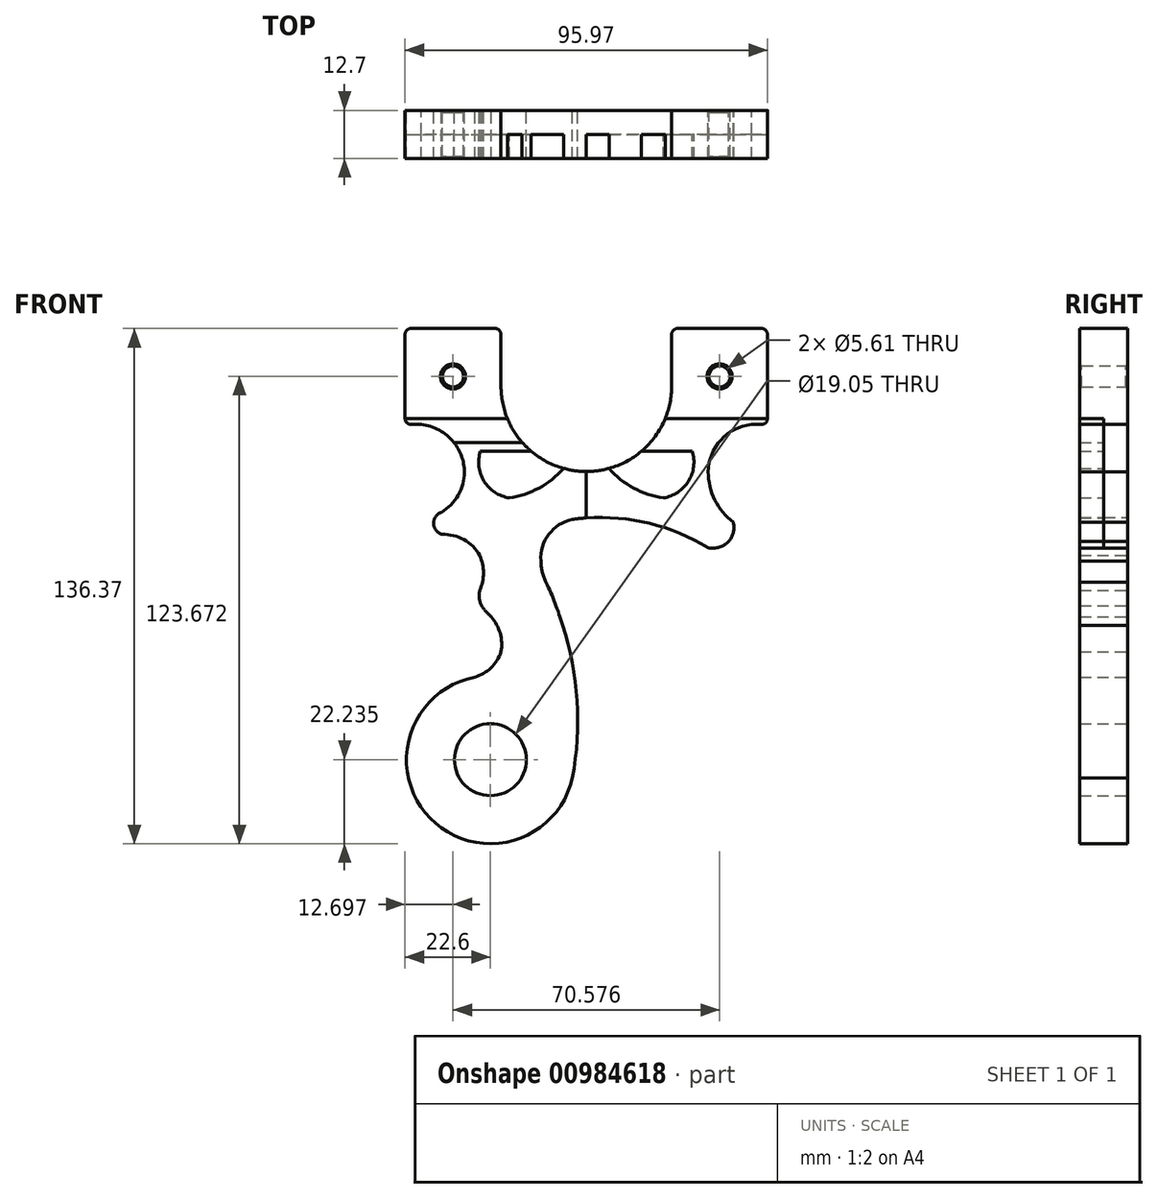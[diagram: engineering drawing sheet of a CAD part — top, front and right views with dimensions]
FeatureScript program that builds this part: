
annotation { "Feature Type Name" : "Feature", "Feature Type Description" : "" }
export const myFeature = defineFeature(function(context is Context, id is Id, definition is map)
    precondition{}
    {
        {
            var Q0;
            Q0=qCreatedBy(makeId("Front.planeOp"),FACE);
            var sketch = newSketch(context, id + "F0", { "sketchPlane" : qUnion([Q0])});
            skCircle(sketch, "E0", {"center": v(-13.36, -38.22) * mm, "radius": 9.53 * mm});
            skLineSegment(sketch, "E1", {"start": v(-35.96, 52.1) * mm, "end": v(-35.96, 74.33) * mm});
            skLineSegment(sketch, "E2.bottom", {"start": v(-34.38, 75.92) * mm, "end": v(-12.15, 75.92) * mm});
            skLineSegment(sketch, "E2.top", {"start": v(-34.38, 50.52) * mm, "end": v(-31.71, 50.52) * mm});
            skLineSegment(sketch, "E2.left", {"start": v(-35.96, 74.33) * mm, "end": v(-35.96, 52.1) * mm});
            skLineSegment(sketch, "E2.right", {"start": v(-10.56, 74.33) * mm, "end": v(-10.56, 60.66) * mm});
            skArc(sketch, "E3", {"start": v(-10.56, 60.66) * mm, "mid": v(-3.95, 44.68) * mm, "end": v(12.03, 38.07) * mm});
            skLineSegment(sketch, "E4", {"start": v(-23.26, 60.42) * mm, "end": v(-23.26, 66.03) * mm});
            skLineSegment(sketch, "E5", {"start": v(-26.07, 63.22) * mm, "end": v(-20.46, 63.22) * mm});
            skCircle(sketch, "E6", {"center": v(-23.26, 63.22) * mm, "radius": 2.8 * mm});
            skCircle(sketch, "E7.MirrorC", {"center": v(47.31, 63.22) * mm, "radius": 2.8 * mm});
            skLineSegment(sketch, "E8.MirrorCS", {"start": v(47.31, 60.42) * mm, "end": v(47.31, 66.03) * mm});
            skLineSegment(sketch, "E9.MirrorCS", {"start": v(50.12, 63.22) * mm, "end": v(44.5, 63.22) * mm});
            skLineSegment(sketch, "E10.MirrorCS", {"start": v(60.01, 74.33) * mm, "end": v(60.01, 52.1) * mm});
            skLineSegment(sketch, "E11.MirrorCS", {"start": v(58.43, 75.92) * mm, "end": v(36.2, 75.92) * mm});
            skLineSegment(sketch, "E12.MirrorCS", {"start": v(34.61, 74.33) * mm, "end": v(34.61, 60.66) * mm});
            skLineSegment(sketch, "E13.MirrorCS", {"start": v(58.43, 50.52) * mm, "end": v(55.76, 50.52) * mm});
            skArc(sketch, "E14.MirrorCS", {"start": v(34.61, 60.66) * mm, "mid": v(28, 44.68) * mm, "end": v(12.03, 38.07) * mm});
            skArc(sketch, "E15", {"start": v(-35.96, 52.1) * mm, "mid": v(-35.5, 50.99) * mm, "end": v(-34.38, 50.52) * mm});
            skArc(sketch, "E16.MirrorC", {"start": v(-35.96, 74.33) * mm, "mid": v(-35.5, 75.46) * mm, "end": v(-34.38, 75.92) * mm});
            skArc(sketch, "E17.MirrorC", {"start": v(-10.56, 74.33) * mm, "mid": v(-11.03, 75.46) * mm, "end": v(-12.15, 75.92) * mm});
            skPoint(sketch, "E18.orphan", {"position": v(-35.96, 75.92) * mm});
            skPoint(sketch, "E19.orphan", {"position": v(-35.96, 50.52) * mm});
            skPoint(sketch, "E20.orphan", {"position": v(-10.56, 75.92) * mm});
            skLineSegment(sketch, "E21.trimOffspring", {"start": v(-12.15, 75.92) * mm, "end": v(-34.38, 75.92) * mm});
            skArc(sketch, "E22.MirrorCS", {"start": v(60.01, 74.33) * mm, "mid": v(59.55, 75.46) * mm, "end": v(58.43, 75.92) * mm});
            skArc(sketch, "E23.MirrorCS", {"start": v(34.61, 74.33) * mm, "mid": v(35.08, 75.46) * mm, "end": v(36.2, 75.92) * mm});
            skArc(sketch, "E24.MirrorCS", {"start": v(60.01, 52.1) * mm, "mid": v(59.55, 50.99) * mm, "end": v(58.43, 50.52) * mm});
            skPoint(sketch, "E25.orphan", {"position": v(34.61, 75.92) * mm});
            skPoint(sketch, "E26.orphan", {"position": v(60.01, 75.92) * mm});
            skPoint(sketch, "E27.orphan", {"position": v(60.01, 50.52) * mm});
            skArc(sketch, "E28", {"start": v(-20.26, 37.95) * mm, "mid": v(-23.6, 46.4) * mm, "end": v(-31.71, 50.52) * mm});
            skArc(sketch, "E29", {"start": v(-26.41, 27.23) * mm, "mid": v(-21.91, 31.78) * mm, "end": v(-20.26, 37.95) * mm});
            skArc(sketch, "E30", {"start": v(-26.41, 27.23) * mm, "mid": v(-28.4, 24.24) * mm, "end": v(-26.16, 21.43) * mm});
            skArc(sketch, "E31.MirrorCS", {"start": v(44.3, 37.95) * mm, "mid": v(47.66, 46.4) * mm, "end": v(55.76, 50.52) * mm});
            skArc(sketch, "E32", {"start": v(44.3, 37.95) * mm, "mid": v(46.08, 30.51) * mm, "end": v(50.92, 24.58) * mm});
            skArc(sketch, "E33", {"start": v(49.74, 19.53) * mm, "mid": v(50.95, 21.91) * mm, "end": v(50.92, 24.58) * mm});
            skArc(sketch, "E34", {"start": v(44.3, 17.9) * mm, "mid": v(47.24, 18) * mm, "end": v(49.74, 19.53) * mm});
            skArc(sketch, "E35", {"start": v(44.3, 17.9) * mm, "mid": v(26.94, 24.73) * mm, "end": v(8.3, 25.39) * mm});
            skArc(sketch, "E36", {"start": v(8.3, 25.39) * mm, "mid": v(2.11, 21.42) * mm, "end": v(0, 14.39) * mm});
            skPoint(sketch, "E37.orphan", {"position": v(-23.26, 75.92) * mm});
            skPoint(sketch, "E38.orphan", {"position": v(-10.56, 63.22) * mm});
            skPoint(sketch, "E39.orphan", {"position": v(-23.26, 50.52) * mm});
            skPoint(sketch, "E40.orphan", {"position": v(-35.96, 63.22) * mm});
            skPoint(sketch, "E41.orphan", {"position": v(-10.56, 50.52) * mm});
            skPoint(sketch, "E42.orphan", {"position": v(34.61, 50.52) * mm});
            skPoint(sketch, "E43.orphan", {"position": v(47.31, 50.52) * mm});
            skPoint(sketch, "E44.orphan", {"position": v(60.01, 63.22) * mm});
            skPoint(sketch, "E45.orphan", {"position": v(47.31, 75.92) * mm});
            skPoint(sketch, "E46.orphan", {"position": v(34.61, 63.22) * mm});
            skArc(sketch, "E47", {"start": v(-16.19, 15.84) * mm, "mid": v(-20.4, 20) * mm, "end": v(-26.16, 21.43) * mm});
            skArc(sketch, "E48", {"start": v(-16.19, 6.57) * mm, "mid": v(-15.22, 11.2) * mm, "end": v(-16.19, 15.84) * mm});
            skArc(sketch, "E49", {"start": v(-16.19, 6.57) * mm, "mid": v(-16.3, 4.5) * mm, "end": v(-15.73, 2.52) * mm});
            skArc(sketch, "E50", {"start": v(-15.73, 2.52) * mm, "mid": v(-14.52, 0.95) * mm, "end": v(-13.1, -0.44) * mm});
            skArc(sketch, "E51", {"start": v(-10.57, -9.67) * mm, "mid": v(-10.8, -4.77) * mm, "end": v(-13.1, -0.44) * mm});
            skArc(sketch, "E52", {"start": v(-17.5, -16.37) * mm, "mid": v(-29.31, -53.7) * mm, "end": v(8.35, -43) * mm});
            skArc(sketch, "E53", {"start": v(-17.5, -16.37) * mm, "mid": v(-13.2, -13.89) * mm, "end": v(-10.57, -9.67) * mm});
            skArc(sketch, "E54", {"start": v(0, 14.39) * mm, "mid": v(0.34, 11.48) * mm, "end": v(1.34, 8.73) * mm});
            skArc(sketch, "E55", {"start": v(5.72, -2.63) * mm, "mid": v(3.78, 3.15) * mm, "end": v(1.34, 8.73) * mm});
            skArc(sketch, "E56", {"start": v(8.35, -43) * mm, "mid": v(9.56, -22.65) * mm, "end": v(5.72, -2.63) * mm});
            skLineSegment(sketch, "E57", {"start": v(-13.36, -38.22) * mm, "end": v(-13.36, -47.74) * mm});
            skLineSegment(sketch, "E58", {"start": v(-13.36, -38.22) * mm, "end": v(-13.36, -28.7) * mm});
            skLineSegment(sketch, "E59", {"start": v(-13.36, -38.22) * mm, "end": v(-3.84, -38.22) * mm});
            skLineSegment(sketch, "E60", {"start": v(-13.36, -38.22) * mm, "end": v(-22.89, -38.22) * mm});
            skCircle(sketch, "E61", {"center": v(-13.36, -38.22) * mm, "radius": 0.8 * mm});
            skSolve(sketch);
        }
        {
            var Q0;
            Q0=qSketchRegion(id+"F0",true);
            extrude(context, id + "F1", {"entities" : qUnion([Q0]), "depth" : 12.7 * mm, "offsetDistance" : 25.4 * mm});
        }
        {
            var Q0;
            Q0=makeQuery(id+"F1.opExtrude","CAP_EDGE",EDGE,{"disambiguationData":[OSD([sQuery(id+"F0.wireOp",EDGE,"E61")])],"isStart":false});
            var Q1;
            Q1=makeQuery(id+"F1.opExtrude","CAP_EDGE",EDGE,{"disambiguationData":[OSD([sQuery(id+"F0.wireOp",EDGE,"E6")])],"isStart":false});
            var Q2;
            Q2=makeQuery(id+"F1.opExtrude","CAP_EDGE",EDGE,{"disambiguationData":[OSD([sQuery(id+"F0.wireOp",EDGE,"E7.MirrorC")])],"isStart":false});
            var Q3;
            Q3=makeQuery(id+"F1.opExtrude","CAP_EDGE",EDGE,{"disambiguationData":[OSD([sQuery(id+"F0.wireOp",EDGE,"E7.MirrorC")])],"isStart":true});
            var Q4;
            Q4=makeQuery(id+"F1.opExtrude","CAP_EDGE",EDGE,{"disambiguationData":[OSD([sQuery(id+"F0.wireOp",EDGE,"E6")])],"isStart":true});
            var Q5;
            Q5=makeQuery(id+"F1.opExtrude","CAP_EDGE",EDGE,{"disambiguationData":[OSD([sQuery(id+"F0.wireOp",EDGE,"E61")])],"isStart":true});
            chamfer(context, id + "F2", {"entities" : qUnion([Q0, Q1, Q2, Q3, Q4, Q5]), "width" : 0.5 * mm, "tangentPropagation" : true});
        }
        {
            var Q0;
            Q0=makeQuery(id+"F1.opExtrude","CAP_FACE",FACE,{"disambiguationData":[OSD([sQuery(id+"F0.wireOp",EDGE,"E0"),sQuery(id+"F0.wireOp",EDGE,"E2.top"),sQuery(id+"F0.wireOp",EDGE,"E2.left"),sQuery(id+"F0.wireOp",EDGE,"E2.right"),sQuery(id+"F0.wireOp",EDGE,"E3"),sQuery(id+"F0.wireOp",EDGE,"E6"),sQuery(id+"F0.wireOp",EDGE,"E7.MirrorC"),sQuery(id+"F0.wireOp",EDGE,"E10.MirrorCS"),sQuery(id+"F0.wireOp",EDGE,"E11.MirrorCS"),sQuery(id+"F0.wireOp",EDGE,"E12.MirrorCS"),sQuery(id+"F0.wireOp",EDGE,"E13.MirrorCS"),sQuery(id+"F0.wireOp",EDGE,"E14.MirrorCS"),sQuery(id+"F0.wireOp",EDGE,"E15"),sQuery(id+"F0.wireOp",EDGE,"E16.MirrorC"),sQuery(id+"F0.wireOp",EDGE,"E17.MirrorC"),sQuery(id+"F0.wireOp",EDGE,"E21.trimOffspring"),sQuery(id+"F0.wireOp",EDGE,"E22.MirrorCS"),sQuery(id+"F0.wireOp",EDGE,"E23.MirrorCS"),sQuery(id+"F0.wireOp",EDGE,"E24.MirrorCS"),sQuery(id+"F0.wireOp",EDGE,"E28"),sQuery(id+"F0.wireOp",EDGE,"E29"),sQuery(id+"F0.wireOp",EDGE,"E30"),sQuery(id+"F0.wireOp",EDGE,"E31.MirrorCS"),sQuery(id+"F0.wireOp",EDGE,"E32"),sQuery(id+"F0.wireOp",EDGE,"E33"),sQuery(id+"F0.wireOp",EDGE,"E34"),sQuery(id+"F0.wireOp",EDGE,"E35"),sQuery(id+"F0.wireOp",EDGE,"E36"),sQuery(id+"F0.wireOp",EDGE,"E47"),sQuery(id+"F0.wireOp",EDGE,"E48"),sQuery(id+"F0.wireOp",EDGE,"E49"),sQuery(id+"F0.wireOp",EDGE,"E50"),sQuery(id+"F0.wireOp",EDGE,"E51"),sQuery(id+"F0.wireOp",EDGE,"E52"),sQuery(id+"F0.wireOp",EDGE,"E53"),sQuery(id+"F0.wireOp",EDGE,"E54"),sQuery(id+"F0.wireOp",EDGE,"E55"),sQuery(id+"F0.wireOp",EDGE,"E56")])],"isStart":false});
            var sketch = newSketch(context, id + "F3", { "sketchPlane" : qUnion([Q0])});
            skLineSegment(sketch, "E62", {"start": v(-35.96, 52.1) * mm, "end": v(60.01, 52.1) * mm});
            skLineSegment(sketch, "E63.0", {"start": v(-35.96, 45.76) * mm, "end": v(60.01, 45.76) * mm});
            skLineSegment(sketch, "E64", {"start": v(12.03, 60.66) * mm, "end": v(12.03, -63.66) * mm});
            skLineSegment(sketch, "E65", {"start": v(9.1, 43.42) * mm, "end": v(-16.03, 43.42) * mm});
            skArc(sketch, "E66", {"start": v(-8.38, 31.06) * mm, "mid": v(1.85, 35.13) * mm, "end": v(9.1, 43.42) * mm});
            skArc(sketch, "E67", {"start": v(-16.03, 43.42) * mm, "mid": v(-15.03, 35.49) * mm, "end": v(-8.38, 31.06) * mm});
            skArc(sketch, "E68.0.0", {"start": v(44.3, 17.9) * mm, "mid": v(47.24, 18) * mm, "end": v(49.74, 19.53) * mm});
            skArc(sketch, "E68.0.1", {"start": v(49.74, 19.53) * mm, "mid": v(50.95, 21.91) * mm, "end": v(50.92, 24.58) * mm});
            skArc(sketch, "E68.0.2", {"start": v(50.92, 24.58) * mm, "mid": v(46.08, 30.51) * mm, "end": v(44.3, 37.95) * mm});
            skArc(sketch, "E68.0.3", {"start": v(44.3, 37.95) * mm, "mid": v(47.66, 46.4) * mm, "end": v(55.76, 50.52) * mm});
            skLineSegment(sketch, "E68.0.4", {"start": v(55.76, 50.52) * mm, "end": v(58.43, 50.52) * mm});
            skArc(sketch, "E68.0.5", {"start": v(58.43, 50.52) * mm, "mid": v(59.55, 50.99) * mm, "end": v(60.01, 52.1) * mm});
            skLineSegment(sketch, "E68.0.6", {"start": v(60.01, 52.1) * mm, "end": v(60.01, 74.33) * mm});
            skArc(sketch, "E68.0.7", {"start": v(60.01, 74.33) * mm, "mid": v(59.55, 75.46) * mm, "end": v(58.43, 75.92) * mm});
            skLineSegment(sketch, "E68.0.8", {"start": v(58.43, 75.92) * mm, "end": v(36.2, 75.92) * mm});
            skArc(sketch, "E68.0.9", {"start": v(36.2, 75.92) * mm, "mid": v(35.08, 75.46) * mm, "end": v(34.61, 74.33) * mm});
            skLineSegment(sketch, "E68.0.10", {"start": v(34.61, 74.33) * mm, "end": v(34.61, 60.66) * mm});
            skArc(sketch, "E68.0.11", {"start": v(34.61, 60.66) * mm, "mid": v(12.03, 38.07) * mm, "end": v(-10.56, 60.66) * mm});
            skLineSegment(sketch, "E68.0.12", {"start": v(-10.56, 60.66) * mm, "end": v(-10.56, 74.33) * mm});
            skArc(sketch, "E68.0.13", {"start": v(-10.56, 74.33) * mm, "mid": v(-11.03, 75.46) * mm, "end": v(-12.15, 75.92) * mm});
            skLineSegment(sketch, "E68.0.14", {"start": v(-12.15, 75.92) * mm, "end": v(-34.38, 75.92) * mm});
            skArc(sketch, "E68.0.15", {"start": v(-34.38, 75.92) * mm, "mid": v(-35.5, 75.46) * mm, "end": v(-35.96, 74.33) * mm});
            skLineSegment(sketch, "E68.0.16", {"start": v(-35.96, 74.33) * mm, "end": v(-35.96, 52.1) * mm});
            skArc(sketch, "E68.0.17", {"start": v(-35.96, 52.1) * mm, "mid": v(-35.5, 50.99) * mm, "end": v(-34.38, 50.52) * mm});
            skLineSegment(sketch, "E68.0.18", {"start": v(-34.38, 50.52) * mm, "end": v(-31.71, 50.52) * mm});
            skArc(sketch, "E68.0.19", {"start": v(-31.71, 50.52) * mm, "mid": v(-23.6, 46.4) * mm, "end": v(-20.26, 37.95) * mm});
            skArc(sketch, "E68.0.20", {"start": v(-20.26, 37.95) * mm, "mid": v(-21.91, 31.78) * mm, "end": v(-26.41, 27.23) * mm});
            skArc(sketch, "E68.0.21", {"start": v(-26.41, 27.23) * mm, "mid": v(-28.4, 24.24) * mm, "end": v(-26.16, 21.43) * mm});
            skArc(sketch, "E68.0.22", {"start": v(-26.16, 21.43) * mm, "mid": v(-20.4, 20) * mm, "end": v(-16.19, 15.84) * mm});
            skArc(sketch, "E68.0.23", {"start": v(-16.19, 15.84) * mm, "mid": v(-15.22, 11.2) * mm, "end": v(-16.19, 6.57) * mm});
            skArc(sketch, "E68.0.24", {"start": v(-16.19, 6.57) * mm, "mid": v(-16.3, 4.5) * mm, "end": v(-15.73, 2.52) * mm});
            skArc(sketch, "E68.0.25", {"start": v(-15.73, 2.52) * mm, "mid": v(-14.52, 0.95) * mm, "end": v(-13.1, -0.44) * mm});
            skArc(sketch, "E68.0.26", {"start": v(-13.1, -0.44) * mm, "mid": v(-10.8, -4.77) * mm, "end": v(-10.57, -9.67) * mm});
            skArc(sketch, "E68.0.27", {"start": v(-10.57, -9.67) * mm, "mid": v(-13.2, -13.89) * mm, "end": v(-17.5, -16.37) * mm});
            skArc(sketch, "E68.0.28", {"start": v(-17.5, -16.37) * mm, "mid": v(-29.31, -53.7) * mm, "end": v(8.35, -43) * mm});
            skArc(sketch, "E68.0.29", {"start": v(8.35, -43) * mm, "mid": v(9.56, -22.65) * mm, "end": v(5.72, -2.63) * mm});
            skArc(sketch, "E68.0.30", {"start": v(5.72, -2.63) * mm, "mid": v(3.78, 3.15) * mm, "end": v(1.34, 8.73) * mm});
            skArc(sketch, "E68.0.31", {"start": v(1.34, 8.73) * mm, "mid": v(0.34, 11.48) * mm, "end": v(0, 14.39) * mm});
            skArc(sketch, "E68.0.32", {"start": v(0, 14.39) * mm, "mid": v(2.11, 21.42) * mm, "end": v(8.3, 25.39) * mm});
            skArc(sketch, "E68.0.33", {"start": v(8.3, 25.39) * mm, "mid": v(26.94, 24.73) * mm, "end": v(44.3, 17.9) * mm});
            skLineSegment(sketch, "E69.MirrorCS", {"start": v(14.95, 43.42) * mm, "end": v(40.08, 43.42) * mm});
            skArc(sketch, "E70.MirrorCS", {"start": v(32.43, 31.06) * mm, "mid": v(22.2, 35.13) * mm, "end": v(14.95, 43.42) * mm});
            skArc(sketch, "E71.MirrorCS", {"start": v(40.08, 43.42) * mm, "mid": v(39.08, 35.49) * mm, "end": v(32.43, 31.06) * mm});
            skSolve(sketch);
        }
        {
            var Q0;
            {var subQ0=sQuery(id+"F3.wireOp",EDGE,"E68.0.17");Q0=makeQuery(id+"F3.imprint","IMPRINT",FACE,{"disambiguationData":[TD([[makeQuery(id+"F3.imprint","IMPRINT",EDGE,{"derivedFrom":subQ0}),1.0]])]});}
            var Q1;
            {var subQ0=sQuery(id+"F3.wireOp",EDGE,"E68.0.4");Q1=makeQuery(id+"F3.imprint","IMPRINT",FACE,{"disambiguationData":[TD([[makeQuery(id+"F3.imprint","IMPRINT",EDGE,{"derivedFrom":subQ0}),-1.0]])]});}
            var Q2;
            {var subQ5=sQuery(id+"F3.wireOp",EDGE,"E71.MirrorCS");Q2=makeQuery(id+"F3.imprint","IMPRINT",FACE,{"disambiguationData":[TD([[makeQuery(id+"F3.imprint","IMPRINT",EDGE,{"derivedFrom":subQ5}),-1.0]])]});}
            var Q3;
            {var subQ0=sQuery(id+"F3.wireOp",EDGE,"E67");Q3=makeQuery(id+"F3.imprint","IMPRINT",FACE,{"disambiguationData":[TD([[makeQuery(id+"F3.imprint","IMPRINT",EDGE,{"derivedFrom":subQ0}),1.0]])]});}
            extrude(context, id + "F4", {"entities" : qUnion([Q0, Q1, Q2, Q3]), "operationType" : NewBodyOperationType.REMOVE, "oppositeDirection" : true, "depth" : 6.35 * mm, "offsetDistance" : 25.4 * mm});
        }
        {
            var Q0;
            Q0=makeQuery(id+"F4.boolean.opBoolean","COPY",FACE,{"derivedFrom":makeQuery(id+"F4.opExtrude","CAP_FACE",FACE,{"disambiguationData":[OSD([sQuery(id+"F3.wireOp",EDGE,"E62"),sQuery(id+"F3.wireOp",EDGE,"E63.0"),sQuery(id+"F3.wireOp",EDGE,"E68.0.11"),sQuery(id+"F3.wireOp",EDGE,"E68.0.17"),sQuery(id+"F3.wireOp",EDGE,"E68.0.18"),sQuery(id+"F3.wireOp",EDGE,"E68.0.19")])],"isStart":false})});
            var Q1;
            Q1=makeQuery(id+"F4.boolean.opBoolean","COPY",FACE,{"derivedFrom":makeQuery(id+"F4.opExtrude","CAP_FACE",FACE,{"disambiguationData":[OSD([sQuery(id+"F3.wireOp",EDGE,"E62"),sQuery(id+"F3.wireOp",EDGE,"E63.0"),sQuery(id+"F3.wireOp",EDGE,"E68.0.3"),sQuery(id+"F3.wireOp",EDGE,"E68.0.4"),sQuery(id+"F3.wireOp",EDGE,"E68.0.5"),sQuery(id+"F3.wireOp",EDGE,"E68.0.11")])],"isStart":false})});
            var Q2;
            Q2=makeQuery(id+"F4.boolean.opBoolean","COPY",FACE,{"derivedFrom":makeQuery(id+"F4.opExtrude","CAP_FACE",FACE,{"disambiguationData":[OSD([sQuery(id+"F3.wireOp",EDGE,"E66"),sQuery(id+"F3.wireOp",EDGE,"E67"),sQuery(id+"F3.wireOp",EDGE,"E68.0.11"),sQuery(id+"F3.wireOp",EDGE,"E65")])],"isStart":false})});
            var Q3;
            Q3=makeQuery(id+"F4.boolean.opBoolean","COPY",FACE,{"derivedFrom":makeQuery(id+"F4.opExtrude","CAP_FACE",FACE,{"disambiguationData":[OSD([sQuery(id+"F3.wireOp",EDGE,"E68.0.11"),sQuery(id+"F3.wireOp",EDGE,"E69.MirrorCS"),sQuery(id+"F3.wireOp",EDGE,"E70.MirrorCS"),sQuery(id+"F3.wireOp",EDGE,"E71.MirrorCS")])],"isStart":false})});
            extrude(context, id + "F5", {"entities" : qUnion([Q0, Q1, Q2, Q3]), "depth" : 6.35 * mm, "offsetDistance" : 25.4 * mm});
        }
    });
